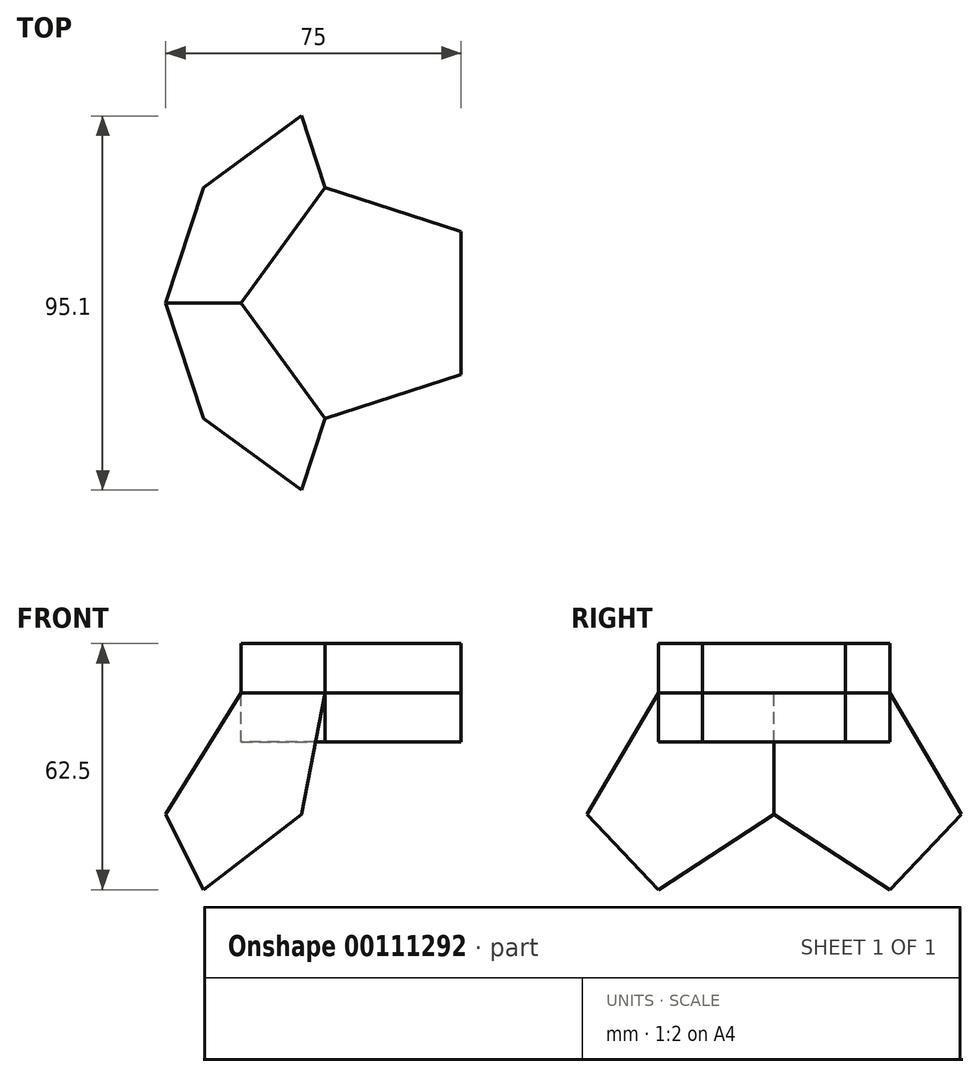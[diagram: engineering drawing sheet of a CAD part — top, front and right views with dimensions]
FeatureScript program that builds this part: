
annotation { "Feature Type Name" : "Feature", "Feature Type Description" : "" }
export const myFeature = defineFeature(function(context is Context, id is Id, definition is map)
    precondition{}
    {
        {
            var Q0;
            Q0=qCreatedBy(makeId("Top.planeOp"),FACE);
            var sketch = newSketch(context, id + "F0", { "sketchPlane" : qUnion([Q0])});
            skCircle(sketch, "E0.cCircle", {"center": v(0, 0) * mm, "radius": 25 * mm, "construction": true});
            skLineSegment(sketch, "E0.0", {"start": v(25, 18.16) * mm, "end": v(25, -18.16) * mm});
            skLineSegment(sketch, "E0.1", {"start": v(25, -18.16) * mm, "end": v(-9.55, -29.39) * mm});
            skLineSegment(sketch, "E0.2", {"start": v(-9.55, -29.39) * mm, "end": v(-30.9, 0) * mm});
            skLineSegment(sketch, "E0.3", {"start": v(-30.9, 0) * mm, "end": v(-9.55, 29.39) * mm});
            skLineSegment(sketch, "E0.4", {"start": v(-9.55, 29.39) * mm, "end": v(25, 18.16) * mm});
            skPoint(sketch, "E0.0.midPoint", {"position": v(25, 0) * mm});
            skLineSegment(sketch, "E1", {"start": v(-30.9, 0) * mm, "end": v(25, 0) * mm, "construction": true});
            skSolve(sketch);
        }
        {
            var Q0;
            Q0=sQuery(id+"F0.wireOp",EDGE,"E0.2");
            var Q1;
            Q1=sQuery(id+"F0.wireOp",EDGE,"E0.3");
            var Q2;
            Q2=sQuery(id+"F0.wireOp",EDGE,"E0.4");
            var Q3;
            Q3=sQuery(id+"F0.wireOp",EDGE,"E0.0");
            var Q4;
            Q4=sQuery(id+"F0.wireOp",EDGE,"E0.1");
            extrude(context, id + "F1", {"bodyType" : ToolBodyType.SURFACE, "surfaceEntities" : qUnion([Q0, Q1, Q2, Q3, Q4]), "endBound" : BoundingType.SYMMETRIC, "depth" : 25 * mm});
        }
        {
            var Q0;
            Q0=qCreatedBy(makeId("Front.planeOp"),FACE);
            var sketch = newSketch(context, id + "F2", { "sketchPlane" : qUnion([Q0])});
            skLineSegment(sketch, "E2.0", {"start": v(-30.9, 0) * mm, "end": v(25, 0) * mm});
            skSolve(sketch);
        }
        {
            var Q0;
            Q0=sQuery(id+"F2.wireOp",EDGE,"E2.0");
            extrude(context, id + "F3", {"bodyType" : ToolBodyType.SURFACE, "surfaceEntities" : qUnion([Q0]), "endBound" : BoundingType.UP_TO_NEXT, "depth" : 25 * mm, "hasSecondDirection" : true, "secondDirectionBound" : SecondDirectionBoundingType.UP_TO_NEXT, "secondDirectionOppositeDirection" : true, "secondDirectionDepth" : 25 * mm});
        }
        {
            var Q0;
            Q0=qCreatedBy(makeId("Front.planeOp"),FACE);
            var sketch = newSketch(context, id + "F4", { "sketchPlane" : qUnion([Q0])});
            skPoint(sketch, "E3.0", {"position": v(-30.9, 0) * mm});
            skLineSegment(sketch, "E4", {"start": v(-30.9, 0) * mm, "end": v(-43, 15.83) * mm});
            skSolve(sketch);
        }
        {
            var Q0;
            Q0=makeQuery(id+"F3.opExtrude","SWEPT_BODY",BODY,{"disambiguationData":[OSD([sQuery(id+"F2.wireOp",EDGE,"E2.0")])]});
            var Q1;
            Q1=sQuery(id+"F4.wireOp",EDGE,"E4");
            circularPattern(context, id + "F5", {"entities" : qUnion([Q0]), "axis" : qUnion([Q1]), "angle" : 360 * degree, "instanceCount" : 3, "equalSpace" : true});
        }
    });
